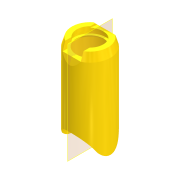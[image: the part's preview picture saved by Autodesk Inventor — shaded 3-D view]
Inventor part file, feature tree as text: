
AUTODESK INVENTOR PART (.ipt)
format: ipt  version: 2020 (Build 240168000, 168)  size: 295,936 bytes
history: native  units: mm
features: sketch x12, extrude x10, revolve x2, plane x2, projected_geometry x2
ambient origin geometry x8: Origin, YZ Plane, XZ Plane, XY Plane, X Axis, Y Axis, Z Axis, Center Point
bodies: Solid1 (feature_tree)
feature tree (28):
  revolve  "Revolution1"  [1 undecoded]
  extrude  "Extrusion1"  Depth=1.1184mm
  extrude  "Extrusion2"  Depth=12.5mm TaperAngle=0.0deg
  extrude  "Extrusion3"  Depth=1.5mm
  extrude  "Extrusion4"  Depth=1.2mm
  plane  "Work Plane1"
  extrude  "Extrusion5"  Depth=24.534mm
  revolve  "Revolution2"  [1 undecoded]
  extrude  "Extrusion6"  Depth=3.99mm
  extrude  "Extrusion7"  Depth=4.6mm
  extrude  "Extrusion8"  Depth=12.5mm TaperAngle=0.0deg
  extrude  "Extrusion9"  Depth=1.239184mm
  plane  "Work Plane2"
  extrude  "Extrusion11"  Depth=18.5mm
  sketch  "Sketch1"  dims[d0=10.33mm d10=2.3mm]
  sketch  "Sketch2"  dims[d11=1.2mm d12=1.1184mm]
  sketch  "Sketch3"  dims[d15=90.0deg d18=12.5mm d19=0.0mm]
  sketch  "Sketch4"  dims[d20=1.5mm d21=1.93mm]
  sketch  "Sketch5"  dims[d22=2.5mm d23=1.2mm]
  sketch  "Sketch6"  dims[d24=4.0mm d25=24.534mm]
  projected_geometry  "Projected Loop1"
  sketch  "Sketch7"  dims[d26=1.45mm d27=0.3547mm]
  sketch  "Sketch8"  dims[d28=4.6mm d29=3.99mm]
  sketch  "Sketch9"  dims[d30=12.5mm d31=0.0mm d32=4.6mm]
  sketch  "Sketch10"  dims[d33=0.62mm d34=12.5mm d35=0.0mm]
  sketch  "Sketch11"  dims[d36=0.01mm d37=0.0mm d38=1.239184mm]
  sketch  "Sketch13"  dims[d39=1.51mm d40=0.551mm d41=0.0mm d42=0.0mm d43=0.808mm d44=1.4269mm d45=90.0deg d46=10.0mm d47=46.75mm d48=0.0mm d49=46.75mm d50=0.0mm d51=2.4mm d52=10.0mm d53=10.125mm d54=0.0mm d55=0.0mm d56=15.5mm d57=0.0mm d61=6.0mm d62=90.0deg d63=6.0mm d64=18.5mm d65=0.0mm]
  projected_geometry  "Projected Loop2"
note: 2 required parameter values undecoded (feature->parameter linkage not recoverable at this tier; creation-order binding heuristic only, values carry confidence <= 0.55)
